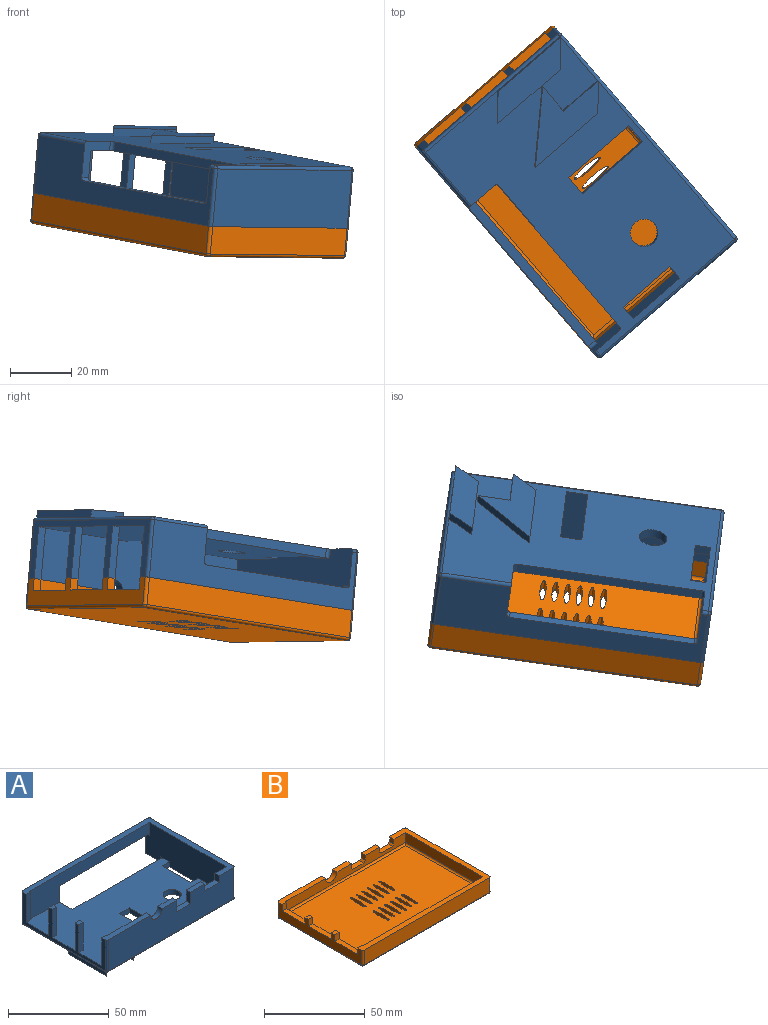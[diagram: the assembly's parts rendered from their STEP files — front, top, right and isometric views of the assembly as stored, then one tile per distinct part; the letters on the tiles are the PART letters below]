
ASSEMBLY  parts=2 mates=2
PART A: 70 faces, bbox 90x60x22.5 mm
  f0: plane 88x58mm, normal (0,0,-1), area 3581.2mm2, adj f12,f17,f19,f20,f21,f22,f23,f24
  f1: plane 3x2.5mm, normal (0,0,1), area 7.5mm2, adj f4,f5,f46,f49
  f2: plane 3x2.5mm, normal (0,0,1), area 7.5mm2, adj f4,f6,f44,f47
  f3: plane 31x3.5mm, normal (0,0,1), area 94.3mm2, adj f4,f7,f11,f12,f43,f45,f55
  f4: plane 58x19mm, normal (-1,0,0), area 286mm2, adj f1,f2,f3,f10,f15,f31,f44,f45
  f5: plane 17x2.5mm, normal (1,0,0), area 42.5mm2, adj f1,f15,f46,f49
  f6: plane 17x2.5mm, normal (1,0,0), area 42.5mm2, adj f2,f15,f44,f47
  f7: plane 17x0.5mm, normal (1,0,0), area 8.5mm2, adj f3,f12,f15,f45
  f8: plane 10x3mm, normal (0,0,1), area 30mm2, adj f11,f12,f41,f43
  f9: plane 10x3mm, normal (0,0,1), area 30mm2, adj f11,f12,f37,f40
  f10: plane 90x60mm, normal (0,0,1), area 465.9mm2, adj f4,f11,f12,f13,f14,f16,f17,f18
  f11: plane 88x19mm, normal (0,-1,0), area 1536.9mm2, adj f3,f8,f9,f10,f30,f37,f38,f39
  f12: plane 84x20mm, normal (0,1,0), area 1313.9mm2, adj f0,f3,f7,f8,f9,f10,f15,f17
  f13: plane 84x17mm, normal (0,-1,0), area 798.4mm2, adj f10,f15,f17,f18,f27,f28,f33,f34
  f14: plane 88x19mm, normal (0,1,0), area 916.4mm2, adj f10,f17,f27,f28,f32,f33,f34,f50
  f15: plane 87x54mm, normal (0,0,1), area 3767mm2, adj f4,f5,f6,f7,f12,f13,f17,f18
  f16: plane 58x19mm, normal (1,0,0), area 1102mm2, adj f10,f29,f50,f57
  f17: plane 57x20mm, normal (-1,0,0), area 1038.3mm2, adj f0,f10,f12,f13,f14,f15,f22,f24
  f18: plane 17x0.5mm, normal (1,0,0), area 8.5mm2, adj f10,f13,f15,f48
  f19: plane 26x3mm, normal (1,0,0), area 78mm2, adj f0,f12,f15,f21
  f20: plane 26x3mm, normal (-1,0,0), area 78mm2, adj f0,f12,f15,f21
  f21: plane 7x3mm, normal (0,-1,0), area 21mm2, adj f0,f15,f19,f20
  f22: plane 5x3mm, normal (0,-1,0), area 15mm2, adj f0,f15,f17,f23
  f23: plane 20.17x3mm, normal (1,0,0), area 60.5mm2, adj f0,f15,f22,f24
  f24: plane 5x3mm, normal (0,1,0), area 15mm2, adj f0,f15,f17,f23
  f25: cylinder r=4.5mm len=9mm, axis (0,0,1), area 84.8mm2, adj f0,f15
  f26: plane 61x3mm, normal (0,1,0), area 183mm2, adj f0,f15,f35,f36
  f27: plane 12x11mm, normal (1,0,0), area 59.8mm2, adj f0,f13,f14,f15,f32,f33,f36
  f28: plane 61x3mm, normal (0,0,-1), area 183mm2, adj f13,f14,f33,f34
  f29: cylinder r=1mm len=58mm, axis (0,1,0), area 91.1mm2, adj f0,f16,f51,f58
  f30: cylinder r=1mm len=88mm, axis (1,0,0), area 138.2mm2, adj f0,f11,f56,f58
  f31: cylinder r=1mm len=58mm, axis (0,-1,0), area 91.1mm2, adj f0,f4,f54,f56,f61
  f32: cylinder r=1mm len=23mm, axis (-1,0,0), area 36.1mm2, adj f0,f14,f27,f54
  f33: cylinder r=1mm len=3mm, axis (0,-1,0), area 4.7mm2, adj f13,f14,f27,f28
  f34: cylinder r=1mm len=3mm, axis (0,-1,0), area 4.7mm2, adj f13,f14,f17,f28
  f35: cylinder r=1mm len=3mm, axis (0,0,1), area 4.7mm2, adj f0,f15,f17,f26
  f36: cylinder r=1mm len=3mm, axis (0,0,1), area 4.7mm2, adj f0,f15,f26,f27
  f37: plane 4x3mm, normal (1,0,0), area 12mm2, adj f9,f11,f12,f38
  f38: plane 10x3mm, normal (0,0,1), area 30mm2, adj f11,f12,f37,f39
  f39: plane 4x3mm, normal (-1,0,0), area 12mm2, adj f10,f11,f12,f38
  f40: plane 7x3mm, normal (-1,0,0), area 21mm2, adj f9,f11,f12,f42
  f41: plane 7x3mm, normal (1,0,0), area 21mm2, adj f8,f11,f12,f42
  f42: plane 10x3mm, normal (0,0,1), area 30mm2, adj f11,f12,f40,f41
  f43: cylinder r=4mm len=8mm, axis (0,-1,0), area 37.7mm2, adj f3,f8,f11,f12
  f44: plane 17x3mm, normal (0,-1,0), area 51mm2, adj f2,f4,f6,f15
  f45: plane 17x3mm, normal (0,1,0), area 51mm2, adj f3,f4,f7,f15
  f46: plane 17x3mm, normal (0,-1,0), area 51mm2, adj f1,f4,f5,f15
  f47: plane 17x3mm, normal (0,1,0), area 51mm2, adj f2,f4,f6,f15
  f48: plane 17x3mm, normal (0,-1,0), area 51mm2, adj f4,f10,f15,f18
  f49: plane 17x3mm, normal (0,1,0), area 51mm2, adj f1,f4,f5,f15
  f50: cylinder r=1mm len=19mm, axis (0,0,1), area 29.8mm2, adj f10,f14,f16,f51
  f51: sphere r=1mm, area 1.6mm2, adj f29,f50,f52
  f52: cylinder r=1mm len=2mm, axis (-1,0,0), area 3.1mm2, adj f0,f14,f17,f51
  f53: cylinder r=1mm len=19mm, axis (0,0,-1), area 29.8mm2, adj f4,f10,f14,f54
  f54: sphere r=1mm, area 1.6mm2, adj f31,f32,f53
  f55: cylinder r=1mm len=19mm, axis (0,0,1), area 29.8mm2, adj f3,f4,f11,f56
  f56: sphere r=1mm, area 1.6mm2, adj f30,f31,f55
  f57: cylinder r=1mm len=19mm, axis (0,0,-1), area 29.8mm2, adj f10,f11,f16,f58
  f58: sphere r=1mm, area 1.6mm2, adj f29,f30,f57
  f59: plane 27x2.5mm, normal (1,0,0), area 67.5mm2, adj f0,f60,f62,f63
  f60: plane 8x7mm, normal (0.66,-0.75,0), area 26.6mm2, adj f0,f59,f61,f63
  f61: plane 27x2.5mm, normal (-1,0,0), area 67.5mm2, adj f31,f60,f62,f63
  f62: plane 8x7mm, normal (-0.66,0.75,0), area 26.6mm2, adj f0,f59,f61,f63
  f63: plane 34x8mm, normal (0,0,-1), area 216mm2, adj f59,f60,f61,f62
  f64: plane 10.5x2.5mm, normal (0,-1,0), area 26.2mm2, adj f0,f65,f68,f69
  f65: plane 19x18.5mm, normal (-0.72,0.7,0), area 66.3mm2, adj f0,f64,f66,f69
  f66: plane 27x2.5mm, normal (1,0,0), area 67.5mm2, adj f0,f65,f67,f69
  f67: plane 8x7mm, normal (0.66,-0.75,0), area 26.6mm2, adj f0,f66,f68,f69
  f68: plane 15x2.5mm, normal (-1,0,0), area 37.5mm2, adj f0,f64,f67,f69
  f69: plane 34x18.5mm, normal (0,0,-1), area 267.7mm2, adj f64,f65,f66,f67,f68
PART B: 64 faces, bbox 90x60x10 mm
  f0: plane 3x2.5mm, normal (0,0,1), area 7.5mm2, adj f3,f13,f54,f59
  f1: plane 3x2.5mm, normal (0,0,1), area 7.5mm2, adj f3,f13,f51,f56
  f2: plane 90x60mm, normal (0,0,1), area 465.9mm2, adj f3,f7,f8,f9,f11,f12,f13,f14
  f3: plane 58x9mm, normal (-1,0,0), area 330mm2, adj f0,f1,f2,f4,f35,f38,f40,f51
  f4: plane 31x3.5mm, normal (0,0,1), area 94.3mm2, adj f3,f7,f12,f13,f38,f50,f57
  f5: plane 10x3mm, normal (0,0,1), area 30mm2, adj f7,f12,f49,f50
  f6: plane 10x3mm, normal (0,0,1), area 30mm2, adj f7,f12,f46,f47
  f7: plane 88x9mm, normal (0,1,0), area 688.9mm2, adj f2,f4,f5,f6,f33,f36,f38,f44
  f8: plane 58x9mm, normal (1,0,0), area 522mm2, adj f2,f32,f36,f42
  f9: plane 88x9mm, normal (0,-1,0), area 792mm2, adj f2,f34,f40,f42
  f10: plane 88x58mm, normal (0,0,-1), area 4896.7mm2, adj f16,f17,f18,f19,f20,f21,f22,f23
  f11: plane 54x6mm, normal (-1,0,0), area 324mm2, adj f2,f12,f14,f29
  f12: plane 84x6mm, normal (0,-1,0), area 400.9mm2, adj f2,f4,f5,f6,f11,f13,f28,f44
  f13: plane 54x6mm, normal (1,0,0), area 132mm2, adj f0,f1,f2,f4,f12,f14,f30,f51
  f14: plane 84x6mm, normal (0,1,0), area 504mm2, adj f2,f11,f13,f31
  f15: plane 82x52mm, normal (0,0,1), area 4056.7mm2, adj f16,f17,f18,f19,f20,f21,f22,f23
  f16: extruded ~11x3mm, area 69mm2, adj f10,f15
  f17: extruded ~11x3mm, area 69mm2, adj f10,f15
  f18: extruded ~11x3mm, area 69mm2, adj f10,f15
  f19: extruded ~11x3mm, area 69mm2, adj f10,f15
  f20: extruded ~11x3mm, area 69mm2, adj f10,f15
  f21: extruded ~11x3mm, area 69mm2, adj f10,f15
  f22: extruded ~11x3mm, area 69mm2, adj f10,f15
  f23: extruded ~11x3mm, area 69mm2, adj f10,f15
  f24: extruded ~11x3mm, area 69mm2, adj f10,f15
  f25: extruded ~11x3mm, area 69mm2, adj f10,f15
  f26: extruded ~11x3mm, area 69mm2, adj f10,f15
  f27: extruded ~11x3mm, area 69mm2, adj f10,f15
  f28: cylinder r=1mm len=84mm, axis (1,0,0), area 130.8mm2, adj f12,f15,f29,f30
  f29: cylinder r=1mm len=54mm, axis (0,-1,0), area 83.7mm2, adj f11,f15,f28,f31
  f30: cylinder r=1mm len=54mm, axis (0,1,0), area 83.7mm2, adj f13,f15,f28,f31
  f31: cylinder r=1mm len=84mm, axis (-1,0,0), area 130.8mm2, adj f14,f15,f29,f30
  f32: cylinder r=1mm len=58mm, axis (0,1,0), area 91.1mm2, adj f8,f10,f37,f43
  f33: cylinder r=1mm len=88mm, axis (-1,0,0), area 138.2mm2, adj f7,f10,f37,f39
  f34: cylinder r=1mm len=88mm, axis (1,0,0), area 138.2mm2, adj f9,f10,f41,f43
  f35: cylinder r=1mm len=58mm, axis (0,-1,0), area 91.1mm2, adj f3,f10,f39,f41
  f36: cylinder r=1mm len=9mm, axis (0,0,1), area 14.1mm2, adj f2,f7,f8,f37
  f37: sphere r=1mm, area 1.6mm2, adj f32,f33,f36
  f38: cylinder r=1mm len=9mm, axis (0,0,-1), area 14.1mm2, adj f3,f4,f7,f39
  f39: sphere r=1mm, area 1.6mm2, adj f33,f35,f38
  f40: cylinder r=1mm len=9mm, axis (0,0,1), area 14.1mm2, adj f2,f3,f9,f41
  f41: sphere r=1mm, area 1.6mm2, adj f34,f35,f40
  f42: cylinder r=1mm len=9mm, axis (0,0,-1), area 14.1mm2, adj f2,f8,f9,f43
  f43: sphere r=1mm, area 1.6mm2, adj f32,f34,f42
  f44: plane 3x3mm, normal (-1,0,0), area 9mm2, adj f2,f7,f12,f63
  f45: plane 8x3mm, normal (0,0,1), area 24mm2, adj f7,f12,f62,f63
  f46: plane 3x3mm, normal (1,0,0), area 9mm2, adj f6,f7,f12,f62
  f47: plane 3x3mm, normal (-1,0,0), area 9mm2, adj f6,f7,f12,f61
  f48: plane 8x3mm, normal (0,0,1), area 24mm2, adj f7,f12,f60,f61
  f49: plane 3x3mm, normal (1,0,0), area 9mm2, adj f5,f7,f12,f60
  f50: cylinder r=4mm len=8mm, axis (0,1,0), area 37.7mm2, adj f4,f5,f7,f12
  f51: plane 4x3mm, normal (0,-1,0), area 12mm2, adj f1,f3,f13,f52
  f52: plane 16x3mm, normal (0,0,1), area 48mm2, adj f3,f13,f51,f53
  f53: plane 4x3mm, normal (0,1,0), area 12mm2, adj f2,f3,f13,f52
  f54: plane 4x3mm, normal (0,-1,0), area 12mm2, adj f0,f3,f13,f55
  f55: plane 16x3mm, normal (0,0,1), area 48mm2, adj f3,f13,f54,f56
  f56: plane 4x3mm, normal (0,1,0), area 12mm2, adj f1,f3,f13,f55
  f57: plane 4x3mm, normal (0,-1,0), area 12mm2, adj f3,f4,f13,f58
  f58: plane 16x3mm, normal (0,0,1), area 48mm2, adj f3,f13,f57,f59
  f59: plane 4x3mm, normal (0,1,0), area 12mm2, adj f0,f3,f13,f58
  f60: plane 3x1mm, normal (0.71,0,0.71), area 4.2mm2, adj f7,f12,f48,f49
  f61: plane 3x1mm, normal (-0.71,0,0.71), area 4.2mm2, adj f7,f12,f47,f48
  f62: plane 3x1mm, normal (0.71,0,0.71), area 4.2mm2, adj f7,f12,f45,f46
  f63: plane 3x1mm, normal (-0.71,0,0.71), area 4.2mm2, adj f7,f12,f44,f45
PLACE A rot(axis=(-0.91,0.42,0.06),177.5deg) t=(-1.54,32.11,150.07)mm
PLACE B rot(axis=(0.05,0.14,-0.99),49.7deg) t=(-4.14,34.72,120.29)mm
MATE parallel B.f15 <-> A.f15  axis (0.09,-0.09,0.99) through (-3.88,34.46,123.27)mm
MATE fastened B.f0 <-> A.f2  axis (0.09,-0.09,0.99) through (-24.46,72.6,135.47)mm
